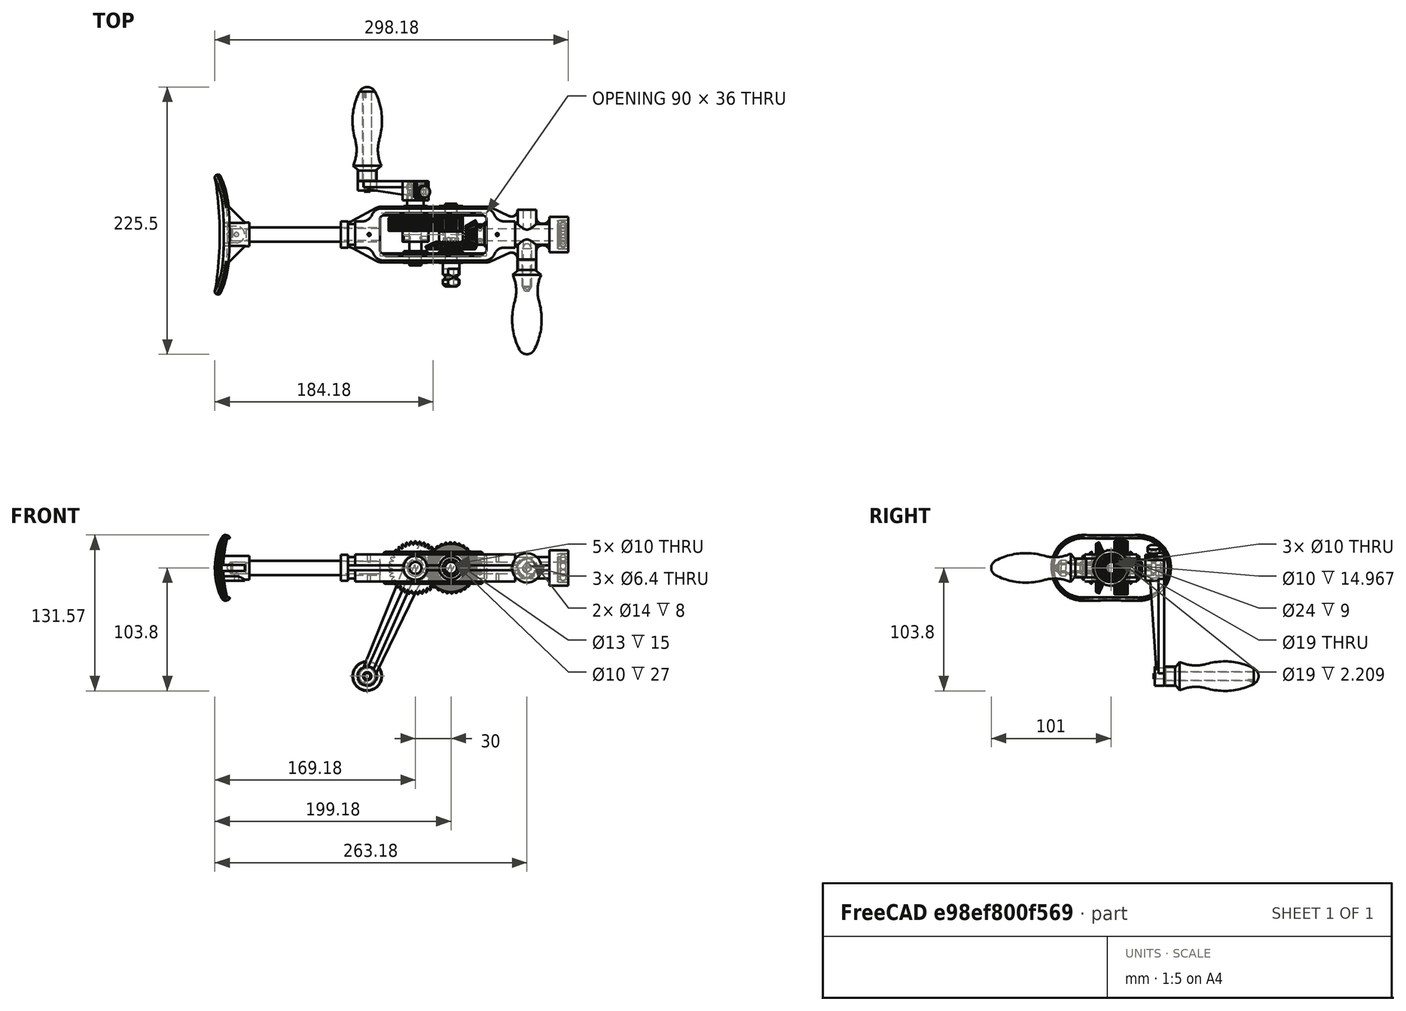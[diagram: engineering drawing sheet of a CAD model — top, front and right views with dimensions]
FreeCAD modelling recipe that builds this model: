
FCSTD DOCUMENT  (FreeCAD 0.18R16146 (Git))
Label: 135 - FURADEIRA_MOV
License: All rights reserved
LicenseURL: http://en.wikipedia.org/wiki/All_rights_reserved
objects: App::FeaturePython×32, Part::FeaturePython×19, Part::Compound×4, App::DocumentObjectGroupPython×4, Part::Cylinder×2, Part::MultiFuse×2
note: 27 computed .brp shape members not serialized (recipe doc carries the construction recipe); baked Part::Feature solids carry a one-line shape summary decoded from their .brp

FEATURE [Part::FeaturePython] import_01  label="1-CHASSI - PEÇA 4_01"  # a2plus imported part (geometry in sourceFile) (typed FeaturePython)
  fixedPosition = true
  sourceFile = <path> MANUAL/1-CHASSI - PEÇA 4.FCStd
  timeLastImport = 1.52112e+09
  updateColors = true
FEATURE [Part::FeaturePython] __ROLAMENTO_01  # a2plus imported part (geometry in sourceFile) (typed FeaturePython)
  Placement = pos=(109.5,0,0) rot=(0,1,0;1.5708rad)
  fixedPosition = false
  sourceFile = <path> MANUAL/2-ROLAMENTO.FCStd
  timeLastImport = 1.52112e+09
  updateColors = true
FEATURE [Part::FeaturePython] __MANDRIL_CJ_01  # a2plus imported part (geometry in sourceFile) (typed FeaturePython)
  Placement = pos=(214,7e-15,0) rot=(0,-1,0;1.5708rad)
  fixedPosition = false
  sourceFile = <path> MANUAL/3-MANDRIL-CJ.FCStd
  timeLastImport = 1.52115e+09
  updateColors = true
FEATURE [App::FeaturePython] circularEdgeConstraint02  label="circularEdgeConstraint02____MANDRIL_CJ_01"  # a2plus constraint (typed FeaturePython)
  Object1 = import_01
  Object2 = __MANDRIL_CJ_01
  SubElement1 = Edge322
  SubElement2 = Edge70
  Type = circularEdge
  directionConstraint = 1
  lockRotation = false
  offset = 0
FEATURE [App::FeaturePython] circularEdgeConstraint02_mirror  label="circularEdgeConstraint02__1-CHASSI - PEÇA 4_01"  # a2plus constraint (typed FeaturePython)
  Object1 = import_01
  Object2 = __MANDRIL_CJ_01
  SubElement1 = Edge322
  SubElement2 = Edge70
  Type = circularEdge
  directionConstraint = 1
  lockRotation = false
  offset = 0
FEATURE [Part::FeaturePython] import_02  label="4-PARAFUSO SEM CABEÇA - PEÇA 7_01"  # a2plus imported part (geometry in sourceFile) (typed FeaturePython)
  Placement = pos=(78.9998,-28,-0.000784469) rot=(-1,0,0;1.5708rad)
  fixedPosition = false
  sourceFile = <path> MANUAL/4-PARAFUSO SEM CABEÇA - PEÇA 7.FCStd
  timeLastImport = 1.52112e+09
  updateColors = true
FEATURE [App::FeaturePython] circularEdgeConstraint03  label="circularEdgeConstraint03__1-CHASSI - PEÇA 4_01"  # a2plus constraint (typed FeaturePython)
  Object1 = import_02
  Object2 = import_01
  SubElement1 = Edge4
  SubElement2 = Face78
  Type = circularEdge
  directionConstraint = 0
  lockRotation = false
  offset = 9
FEATURE [App::FeaturePython] circularEdgeConstraint03_mirror  label="circularEdgeConstraint03__4-PARAFUSO SEM CABEÇA - PEÇA 7_01"  # a2plus constraint (typed FeaturePython)
  Object1 = import_02
  Object2 = import_01
  SubElement1 = Edge4
  SubElement2 = Face78
  Type = circularEdge
  directionConstraint = 0
  lockRotation = false
  offset = 9
FEATURE [Part::FeaturePython] import_03  label="5-CAPA DA BASE DO PUNHO - PEÇA 25_01"  # a2plus imported part (geometry in sourceFile) (typed FeaturePython)
  Placement = pos=(79,-21,0) rot=(1,0,0;1.5708rad)
  fixedPosition = false
  sourceFile = <path> MANUAL/5-CAPA DA BASE DO PUNHO - PEÇA 25.FCStd
  timeLastImport = 1.52112e+09
  updateColors = true
FEATURE [App::FeaturePython] circularEdgeConstraint04  label="circularEdgeConstraint04__5-CAPA DA BASE DO PUNHO - PEÇA 25_01"  # a2plus constraint (typed FeaturePython)
  Object1 = import_01
  Object2 = import_03
  SubElement1 = Edge313
  SubElement2 = Edge3
  Type = circularEdge
  directionConstraint = 0
  lockRotation = false
  offset = 0
FEATURE [App::FeaturePython] circularEdgeConstraint04_mirror  label="circularEdgeConstraint04__1-CHASSI - PEÇA 4_01"  # a2plus constraint (typed FeaturePython)
  Object1 = import_01
  Object2 = import_03
  SubElement1 = Edge313
  SubElement2 = Edge3
  Type = circularEdge
  directionConstraint = 0
  lockRotation = false
  offset = 0
FEATURE [Part::FeaturePython] import_04  label="6-PUNHO FIXO - PEÇA 8_01"  # a2plus imported part (geometry in sourceFile) (typed FeaturePython)
  Placement = pos=(79,-94,-2.1e-14) rot=(-1,0,0;1.5708rad)
  fixedPosition = false
  sourceFile = <path> MANUAL/6-PUNHO FIXO - PEÇA 8.FCStd
  timeLastImport = 1.52112e+09
  updateColors = true
FEATURE [App::FeaturePython] circularEdgeConstraint05  label="circularEdgeConstraint05__5-CAPA DA BASE DO PUNHO - PEÇA 25_01"  # a2plus constraint (typed FeaturePython)
  Object1 = import_04
  Object2 = import_03
  SubElement1 = Edge6
  SubElement2 = Edge11
  Type = circularEdge
  directionConstraint = 1
  lockRotation = false
  offset = 0
FEATURE [App::FeaturePython] circularEdgeConstraint05_mirror  label="circularEdgeConstraint05__6-PUNHO FIXO - PEÇA 8_01"  # a2plus constraint (typed FeaturePython)
  Object1 = import_04
  Object2 = import_03
  SubElement1 = Edge6
  SubElement2 = Edge11
  Type = circularEdge
  directionConstraint = 1
  lockRotation = false
  offset = 0
FEATURE [Part::FeaturePython] import_05  label="7-HASTE DO ENCOSTO - PEÇA 3_01"  # a2plus imported part (geometry in sourceFile) (typed FeaturePython)
  Placement = pos=(-170,-1.6e-14,3.8e-14) rot=(0,-1,0;1.5708rad)
  fixedPosition = false
  sourceFile = <path> MANUAL/7-HASTE DO ENCOSTO - PEÇA 3.FCStd
  timeLastImport = 1.52112e+09
  updateColors = true
FEATURE [App::FeaturePython] circularEdgeConstraint06  label="circularEdgeConstraint06__1-CHASSI - PEÇA 4_01"  # a2plus constraint (typed FeaturePython)
  Object1 = import_05
  Object2 = import_01
  SubElement1 = Edge11
  SubElement2 = Edge106
  Type = circularEdge
  directionConstraint = 1
  lockRotation = false
  offset = 0
FEATURE [App::FeaturePython] circularEdgeConstraint06_mirror  label="circularEdgeConstraint06__7-HASTE DO ENCOSTO - PEÇA 3_01"  # a2plus constraint (typed FeaturePython)
  Object1 = import_05
  Object2 = import_01
  SubElement1 = Edge11
  SubElement2 = Edge106
  Type = circularEdge
  directionConstraint = 1
  lockRotation = false
  offset = 0
FEATURE [Part::FeaturePython] import_06  label="8-ENCOSTO - PEÇA 1_01"  # a2plus imported part (geometry in sourceFile) (typed FeaturePython)
  Placement = pos=(-460,-9.4e-14,2.5e-14) rot=(0.57735,0.57735,-0.57735;2.0944rad)
  fixedPosition = false
  sourceFile = <path> MANUAL/8-ENCOSTO - PEÇA 1.FCStd
  timeLastImport = 1.52112e+09
  updateColors = true
FEATURE [App::FeaturePython] circularEdgeConstraint07  label="circularEdgeConstraint07__7-HASTE DO ENCOSTO - PEÇA 3_01"  # a2plus constraint (typed FeaturePython)
  Object1 = import_06
  Object2 = import_05
  SubElement1 = Edge13
  SubElement2 = Edge6
  Type = circularEdge
  directionConstraint = 1
  lockRotation = true
  offset = 0
FEATURE [App::FeaturePython] circularEdgeConstraint07_mirror  label="circularEdgeConstraint07__8-ENCOSTO - PEÇA 1_01"  # a2plus constraint (typed FeaturePython)
  Object1 = import_06
  Object2 = import_05
  SubElement1 = Edge13
  SubElement2 = Edge6
  Type = circularEdge
  directionConstraint = 1
  lockRotation = true
  offset = 0
FEATURE [Part::FeaturePython] import_07  label="9-EIXO INF- SUP -PEÇA 5 e 6_01"  # a2plus imported part (geometry in sourceFile) (typed FeaturePython)
  Placement = pos=(15,26,-4e-15) rot=(1,0,0;1.5708rad)
  fixedPosition = false
  sourceFile = <path> MANUAL/9-EIXO INF- SUP -PEÇA 5 e 6.FCStd
  timeLastImport = 1.52112e+09
  updateColors = true
FEATURE [App::FeaturePython] circularEdgeConstraint08  label="circularEdgeConstraint08__9-EIXO INF- SUP -PEÇA 5 e 6_01"  # a2plus constraint (typed FeaturePython)
  Object1 = import_01
  Object2 = import_07
  SubElement1 = Edge130
  SubElement2 = Edge39
  Type = circularEdge
  directionConstraint = 1
  lockRotation = false
  offset = 0
FEATURE [App::FeaturePython] circularEdgeConstraint08_mirror  label="circularEdgeConstraint08__1-CHASSI - PEÇA 4_01"  # a2plus constraint (typed FeaturePython)
  Object1 = import_01
  Object2 = import_07
  SubElement1 = Edge130
  SubElement2 = Edge39
  Type = circularEdge
  directionConstraint = 1
  lockRotation = false
  offset = 0
FEATURE [Part::FeaturePython] import_08  label="9-EIXO INF- SUP -PEÇA 5 e 6_02"  # a2plus imported part (geometry in sourceFile) (typed FeaturePython)
  Placement = pos=(-15,-26,7e-15) rot=(-1,0,0;1.5708rad)
  fixedPosition = false
  sourceFile = <path> MANUAL/9-EIXO INF- SUP -PEÇA 5 e 6.FCStd
  timeLastImport = 1.52112e+09
  updateColors = true
FEATURE [Part::FeaturePython] _0_ENGRENAGEM_1_1_01  # a2plus imported part (geometry in sourceFile) (typed FeaturePython)
  Placement = pos=(-15,14,1e-15) rot=(1,0,0;1.5708rad)
  fixedPosition = false
  sourceFile = <path> MANUAL/10-ENGRENAGEM 1-1.FCStd
  timeLastImport = 1.52114e+09
  updateColors = true
FEATURE [App::FeaturePython] circularEdgeConstraint10  label="circularEdgeConstraint10___0_ENGRENAGEM_1_1_01"  # a2plus constraint (typed FeaturePython)
  Object1 = import_01
  Object2 = _0_ENGRENAGEM_1_1_01
  SubElement1 = Edge136
  SubElement2 = Edge13
  Type = circularEdge
  directionConstraint = 0
  lockRotation = false
  offset = 0
FEATURE [App::FeaturePython] circularEdgeConstraint10_mirror  label="circularEdgeConstraint10__1-CHASSI - PEÇA 4_01"  # a2plus constraint (typed FeaturePython)
  Object1 = import_01
  Object2 = _0_ENGRENAGEM_1_1_01
  SubElement1 = Edge136
  SubElement2 = Edge13
  Type = circularEdge
  directionConstraint = 0
  lockRotation = false
  offset = 0
FEATURE [Part::FeaturePython] _1_ENGRENAGEM_1_2_01  # a2plus imported part (geometry in sourceFile) (typed FeaturePython)
  Placement = pos=(15,-0.125049,0) rot=(-1,0,0;1.5708rad)
  fixedPosition = false
  sourceFile = <path> MANUAL/11-ENGRENAGEM 1-2.FCStd
  timeLastImport = 1.52114e+09
  updateColors = true
FEATURE [App::FeaturePython] circularEdgeConstraint11  label="circularEdgeConstraint11__1-CHASSI - PEÇA 4_01"  # a2plus constraint (typed FeaturePython)
  Object1 = _1_ENGRENAGEM_1_2_01
  Object2 = import_01
  SubElement1 = Edge3
  SubElement2 = Edge239
  Type = circularEdge
  directionConstraint = 0
  lockRotation = false
  offset = 1.5
FEATURE [App::FeaturePython] circularEdgeConstraint11_mirror  label="circularEdgeConstraint11___1_ENGRENAGEM_1_2_01"  # a2plus constraint (typed FeaturePython)
  Object1 = _1_ENGRENAGEM_1_2_01
  Object2 = import_01
  SubElement1 = Edge3
  SubElement2 = Edge239
  Type = circularEdge
  directionConstraint = 0
  lockRotation = false
  offset = 1.5
FEATURE [Part::FeaturePython] _3_ENGRENAGEM_2_1_01  # a2plus imported part (geometry in sourceFile) (typed FeaturePython)
  Placement = pos=(15.0003,0,9e-15) rot=(-0.129428,-0.983106,0.129428;1.58783rad)
  fixedPosition = false
  sourceFile = <path> MANUAL/13-ENGRENAGEM 2-1.FCStd
  timeLastImport = 1.52115e+09
  updateColors = true
FEATURE [App::FeaturePython] circularEdgeConstraint12  label="circularEdgeConstraint12__1-CHASSI - PEÇA 4_01"  # a2plus constraint (typed FeaturePython)
  Object1 = _3_ENGRENAGEM_2_1_01
  Object2 = import_01
  SubElement1 = Edge12
  SubElement2 = Edge1
  Type = circularEdge
  directionConstraint = 1
  lockRotation = true
  offset = 0
FEATURE [App::FeaturePython] circularEdgeConstraint12_mirror  label="circularEdgeConstraint12___3_ENGRENAGEM_2_1_01"  # a2plus constraint (typed FeaturePython)
  Object1 = _3_ENGRENAGEM_2_1_01
  Object2 = import_01
  SubElement1 = Edge12
  SubElement2 = Edge1
  Type = circularEdge
  directionConstraint = 1
  lockRotation = true
  offset = 0
FEATURE [Part::FeaturePython] _3_ENGRENAGEM_2_2_01  # a2plus imported part (geometry in sourceFile) (typed FeaturePython)
  Placement = pos=(15,14,-2e-15) rot=(1,0,0;1.5708rad)
  fixedPosition = false
  sourceFile = <path> MANUAL/13-ENGRENAGEM 2-2.FCStd
  timeLastImport = 1.52114e+09
  updateColors = true
FEATURE [App::FeaturePython] circularEdgeConstraint13  label="circularEdgeConstraint13__1-CHASSI - PEÇA 4_01"  # a2plus constraint (typed FeaturePython)
  Object1 = _3_ENGRENAGEM_2_2_01
  Object2 = import_01
  SubElement1 = Edge13
  SubElement2 = Edge150
  Type = circularEdge
  directionConstraint = 0
  lockRotation = false
  offset = 0
FEATURE [App::FeaturePython] circularEdgeConstraint13_mirror  label="circularEdgeConstraint13___3_ENGRENAGEM_2_2_01"  # a2plus constraint (typed FeaturePython)
  Object1 = _3_ENGRENAGEM_2_2_01
  Object2 = import_01
  SubElement1 = Edge13
  SubElement2 = Edge150
  Type = circularEdge
  directionConstraint = 0
  lockRotation = false
  offset = 0
FEATURE [Part::FeaturePython] import_09  label="14-MANIVELA - PEÇA 22_01"  # a2plus imported part (geometry in sourceFile) (typed FeaturePython)
  Placement = pos=(-15,45,-9e-15) rot=(0,0.707107,-0.707107;3.14159rad)
  fixedPosition = false
  sourceFile = <path> MANUAL/14-MANIVELA - PEÇA 22.FCStd
  timeLastImport = 1.52112e+09
  updateColors = true
FEATURE [App::FeaturePython] circularEdgeConstraint14  label="circularEdgeConstraint14__14-MANIVELA - PEÇA 22_01"  # a2plus constraint (typed FeaturePython)
  Object1 = import_01
  Object2 = import_09
  SubElement1 = Edge139
  SubElement2 = Edge37
  Type = circularEdge
  directionConstraint = 1
  lockRotation = false
  offset = -5
FEATURE [App::FeaturePython] circularEdgeConstraint14_mirror  label="circularEdgeConstraint14__1-CHASSI - PEÇA 4_01"  # a2plus constraint (typed FeaturePython)
  Object1 = import_01
  Object2 = import_09
  SubElement1 = Edge139
  SubElement2 = Edge37
  Type = circularEdge
  directionConstraint = 1
  lockRotation = false
  offset = -5
FEATURE [Part::FeaturePython] import_10  label="5-CAPA DA BASE DO PUNHO - PEÇA 25_02"  # a2plus imported part (geometry in sourceFile) (typed FeaturePython)
  Placement = pos=(-15,45,100) rot=(0,0.707107,0.707107;3.14159rad)
  fixedPosition = false
  sourceFile = <path> MANUAL/5-CAPA DA BASE DO PUNHO - PEÇA 25.FCStd
  timeLastImport = 1.52112e+09
  updateColors = true
FEATURE [App::FeaturePython] circularEdgeConstraint15  label="circularEdgeConstraint15__5-CAPA DA BASE DO PUNHO - PEÇA 25_02"  # a2plus constraint (typed FeaturePython)
  Object1 = import_09
  Object2 = import_10
  SubElement1 = Edge67
  SubElement2 = Edge3
  Type = circularEdge
  directionConstraint = 0
  lockRotation = false
  offset = 0
FEATURE [App::FeaturePython] circularEdgeConstraint15_mirror  label="circularEdgeConstraint15__14-MANIVELA - PEÇA 22_01"  # a2plus constraint (typed FeaturePython)
  Object1 = import_09
  Object2 = import_10
  SubElement1 = Edge67
  SubElement2 = Edge3
  Type = circularEdge
  directionConstraint = 0
  lockRotation = false
  offset = 0
FEATURE [Part::FeaturePython] _5_PUNHO_MOVEL_01  # a2plus imported part (geometry in sourceFile) (typed FeaturePython)
  Placement = pos=(-15,118,100) rot=(1,0,0;1.5708rad)
  fixedPosition = false
  sourceFile = <path> MANUAL/15-PUNHO MOVEL.FCStd
  timeLastImport = 1.52115e+09
  updateColors = true
FEATURE [App::FeaturePython] circularEdgeConstraint16  label="circularEdgeConstraint16___5_PUNHO_MOVEL_01"  # a2plus constraint (typed FeaturePython)
  Object1 = import_10
  Object2 = _5_PUNHO_MOVEL_01
  SubElement1 = Edge11
  SubElement2 = Edge5
  Type = circularEdge
  directionConstraint = 1
  lockRotation = false
  offset = 0
FEATURE [App::FeaturePython] circularEdgeConstraint16_mirror  label="circularEdgeConstraint16__5-CAPA DA BASE DO PUNHO - PEÇA 25_02"  # a2plus constraint (typed FeaturePython)
  Object1 = import_10
  Object2 = _5_PUNHO_MOVEL_01
  SubElement1 = Edge11
  SubElement2 = Edge5
  Type = circularEdge
  directionConstraint = 1
  lockRotation = false
  offset = 0
FEATURE [Part::FeaturePython] import_11  label="16-PINO DE EXPULSÃO - PEÇA 14_01"  # a2plus imported part (geometry in sourceFile) (typed FeaturePython)
  Placement = pos=(-15.0002,36,-19) rot=(0,0,1;0rad)
  fixedPosition = false
  sourceFile = <path> MANUAL/16-PINO DE EXPULSÃO - PEÇA 14.FCStd
  timeLastImport = 1.52112e+09
  updateColors = true
FEATURE [App::FeaturePython] circularEdgeConstraint17  label="circularEdgeConstraint17__16-PINO DE EXPULSÃO - PEÇA 14_01"  # a2plus constraint (typed FeaturePython)
  Object1 = import_09
  Object2 = import_11
  SubElement1 = Edge12
  SubElement2 = Edge3
  Type = circularEdge
  directionConstraint = 0
  lockRotation = false
  offset = -5
FEATURE [App::FeaturePython] circularEdgeConstraint17_mirror  label="circularEdgeConstraint17__14-MANIVELA - PEÇA 22_01"  # a2plus constraint (typed FeaturePython)
  Object1 = import_09
  Object2 = import_11
  SubElement1 = Edge12
  SubElement2 = Edge3
  Type = circularEdge
  directionConstraint = 0
  lockRotation = false
  offset = -5
FEATURE [Part::FeaturePython] import_12  label="17-PINO DO PUNHO - PEÇA 24_01"  # a2plus imported part (geometry in sourceFile) (typed FeaturePython)
  Placement = pos=(-15,120.5,100) rot=(-1,0,0;1.5708rad)
  fixedPosition = false
  sourceFile = <path> MANUAL/17-PINO DO PUNHO - PEÇA 24.FCStd
  timeLastImport = 1.52112e+09
  updateColors = true
FEATURE [App::FeaturePython] circularEdgeConstraint18  label="circularEdgeConstraint18___5_PUNHO_MOVEL_01"  # a2plus constraint (typed FeaturePython)
  Object1 = import_12
  Object2 = _5_PUNHO_MOVEL_01
  SubElement1 = Edge12
  SubElement2 = Edge4
  Type = circularEdge
  directionConstraint = 0
  lockRotation = false
  offset = 0
FEATURE [App::FeaturePython] circularEdgeConstraint18_mirror  label="circularEdgeConstraint18__17-PINO DO PUNHO - PEÇA 24_01"  # a2plus constraint (typed FeaturePython)
  Object1 = import_12
  Object2 = _5_PUNHO_MOVEL_01
  SubElement1 = Edge12
  SubElement2 = Edge4
  Type = circularEdge
  directionConstraint = 0
  lockRotation = false
  offset = 0
FEATURE [Part::Compound] Compound  label="BASE"
  Links = -> [import_01,__ROLAMENTO_01,import_02,import_03,import_04,import_05,import_06]
FEATURE [Part::Compound] Compound001  label="E3 - 17"
  Links = -> [__MANDRIL_CJ_01,_3_ENGRENAGEM_2_1_01]
  Placement = pos=(0,0,0) rot=(1,0,0;0.865683rad)
FEATURE [Part::Compound] Compound002
  Links = -> [import_07,_1_ENGRENAGEM_1_2_01,_3_ENGRENAGEM_2_2_01]
  Placement = pos=(-15,0,0) rot=(0,0,1;0rad)
FEATURE [Part::Compound] Compound003
  Links = -> [import_08,_0_ENGRENAGEM_1_1_01,import_09,import_10,_5_PUNHO_MOVEL_01,import_11,import_12]
  Placement = pos=(15,0,0) rot=(0,0,1;0rad)
FEATURE [Part::Cylinder] Cylinder
  Angle = 360
  AttacherType = Attacher::AttachEngine3D
  Height = 10
  Placement = pos=(0,0,0) rot=(-1,0,0;1.5708rad)
  Radius = 2
FEATURE [Part::MultiFuse] Fusion  label="E_2 - 15 -34"
  Placement = pos=(15,0,0) rot=(0,1,0;0.432842rad)
  Shapes = -> [Cylinder,Compound002]
FEATURE [Part::Cylinder] Cylinder001
  Angle = 360
  AttacherType = Attacher::AttachEngine3D
  Height = 10
  Placement = pos=(0,0,0) rot=(1,0,0;1.5708rad)
  Radius = 2
FEATURE [Part::MultiFuse] Fusion001  label="E_1 - 37"
  Placement = pos=(-15,0,0) rot=(0,1,0;3.56047rad)
  Shapes = -> [Cylinder001,Compound003]
FEATURE [App::DocumentObjectGroupPython] My_Placer  # scripted group (container) (typed FeaturePython)
  Placement = pos=(-15,0,0) rot=(0,1,0;-2.72271rad)
  RotAxis = (0,1,0)
  RotCenter = (0,0,0)
  arc = -time*100
  arc0 = 0
  arc1 = 90
  target = -> Fusion001
  time = 1.56
  x = -15
  x0 = 0
  x1 = 200
  y = 0
  y0 = 0
  y1 = 0
  z = 0
  z0 = 0
  z1 = 0
FEATURE [App::DocumentObjectGroupPython] My_Placer001  # scripted group (container) (typed FeaturePython)
  Placement = pos=(15,0,0) rot=(0,1,0;6.71603rad)
  RotAxis = (0,1,0)
  RotCenter = (0,0,0)
  arc = time*100*37/15
  arc0 = 0
  arc1 = 90
  target = -> Fusion
  time = 1.56
  x = 15
  x0 = 0
  x1 = 200
  y = 0
  y0 = 0
  y1 = 0
  z = 0
  z0 = 0
  z1 = 0
FEATURE [App::DocumentObjectGroupPython] My_Placer002  # scripted group (container) (typed FeaturePython)
  Placement = pos=(0,0,0) rot=(1,0,0;13.4321rad)
  RotAxis = (1,0,0)
  RotCenter = (0,0,0)
  arc = time*100*37/15*34/17
  arc0 = 0
  arc1 = 90
  target = -> Compound001
  time = 1.56
  x = 0
  x0 = 0
  x1 = 200
  y = 0
  y0 = 0
  y1 = 0
  z = 0
  z0 = 0
  z1 = 0
FEATURE [App::DocumentObjectGroupPython] My_Manager  # scripted group (container) (typed FeaturePython)
  Group = -> [My_Placer,My_Placer001,My_Placer002]
  intervall = 1000
  sleeptime = 0.02
  start = 0
  step = 157
  text = NO
note: 19 file-system paths scrubbed to <path> (originals preserved in the JSON sidecar)
